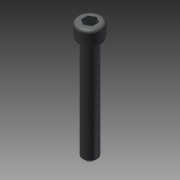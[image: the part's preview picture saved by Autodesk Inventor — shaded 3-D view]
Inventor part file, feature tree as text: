
AUTODESK INVENTOR PART (.ipt)
format: ipt  version: 2015 (Build 190159000, 159)  size: 115,200 bytes
history: native  units: in
note: dims shown in document units (in); Inventor stores cm internally (conversion verified against a paired STEP export)
features: other x6, extrude x1, chamfer x1, sketch x1
ambient origin geometry x8: Origin, YZ Plane, XZ Plane, XY Plane, X Axis, Y Axis, Z Axis, Center Point
bodies: Solid1 (feature_tree)
feature tree (9):
  other  "Screw 1.5in - 739195.ipt"
  extrude  "Extrusion1"  Depth=0.5in TaperAngle=0.0deg
  chamfer  "Chamfer1"  Distance=0.035in Angle=45.0deg
  other  "tetrix_739195_2013::Screw 1.5in - 739195.ipt"
  other  "TaggingFeature1"
  other  "FRONT"
  other  "TOP"
  other  "RIGHT"
  sketch  "Sketch1"  dims[d0=0.3937in d1=0.5in d2=0.0in d3=0.035in d4=0.125in d5=45.0deg]
